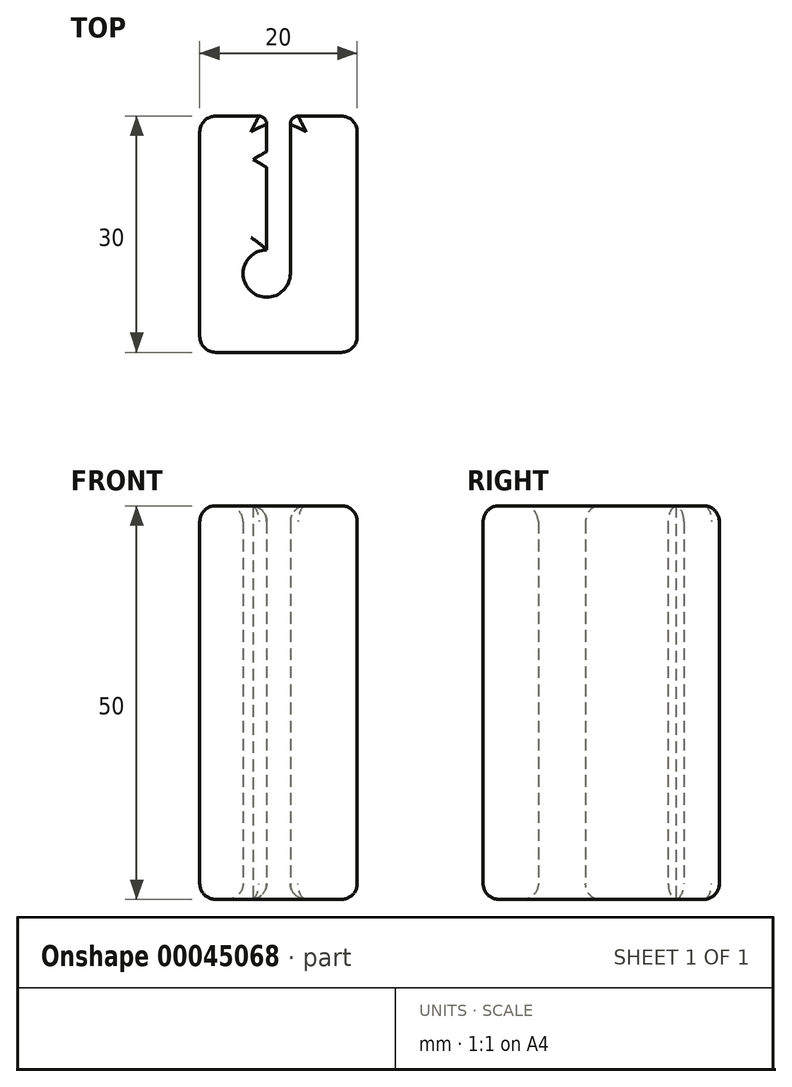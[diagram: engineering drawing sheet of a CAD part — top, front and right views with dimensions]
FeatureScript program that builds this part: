
annotation { "Feature Type Name" : "Feature", "Feature Type Description" : "" }
export const myFeature = defineFeature(function(context is Context, id is Id, definition is map)
    precondition{}
    {
        {
            var Q0;
            Q0=qCreatedBy(makeId("Top.planeOp"),FACE);
            var sketch = newSketch(context, id + "F0", { "sketchPlane" : qUnion([Q0])});
            skLineSegment(sketch, "E0.rect.bottom", {"start": v(8, -15) * mm, "end": v(-8, -15) * mm});
            skLineSegment(sketch, "E0.rect.left", {"start": v(10, -13) * mm, "end": v(10, 13) * mm});
            skLineSegment(sketch, "E0.rect.right", {"start": v(-10, -13) * mm, "end": v(-10, 13) * mm});
            skPoint(sketch, "E0.rect.middle", {"position": v(0, 0) * mm});
            skLineSegment(sketch, "E1.left", {"start": v(-1.5, 14) * mm, "end": v(-1.5, 10.5) * mm});
            skLineSegment(sketch, "E1.right", {"start": v(1.5, 14) * mm, "end": v(1.5, -5) * mm});
            skArc(sketch, "E2", {"start": v(-1.5, -2) * mm, "mid": v(-3.62, -7.12) * mm, "end": v(1.5, -5) * mm});
            skLineSegment(sketch, "E3", {"start": v(2.5, 15) * mm, "end": v(8, 15) * mm});
            skLineSegment(sketch, "E4", {"start": v(-2.5, 15) * mm, "end": v(-8, 15) * mm});
            skPoint(sketch, "E5.visualSharp", {"position": v(-10, 15) * mm});
            skArc(sketch, "E5.filletArc", {"start": v(-8, 15) * mm, "mid": v(-9.41, 14.41) * mm, "end": v(-10, 13) * mm});
            skPoint(sketch, "E6.visualSharp", {"position": v(-10, -15) * mm});
            skArc(sketch, "E6.filletArc", {"start": v(-10, -13) * mm, "mid": v(-9.41, -14.41) * mm, "end": v(-8, -15) * mm});
            skPoint(sketch, "E7.visualSharp", {"position": v(10, -15) * mm});
            skArc(sketch, "E7.filletArc", {"start": v(8, -15) * mm, "mid": v(9.41, -14.41) * mm, "end": v(10, -13) * mm});
            skPoint(sketch, "E8.visualSharp", {"position": v(10, 15) * mm});
            skArc(sketch, "E8.filletArc", {"start": v(10, 13) * mm, "mid": v(9.41, 14.41) * mm, "end": v(8, 15) * mm});
            skPoint(sketch, "E9.visualSharp", {"position": v(1.5, 15) * mm});
            skArc(sketch, "E9.filletArc", {"start": v(2.5, 15) * mm, "mid": v(1.8, 14.7) * mm, "end": v(1.5, 14) * mm});
            skPoint(sketch, "E10.visualSharp", {"position": v(-1.5, 15) * mm});
            skArc(sketch, "E10.filletArc", {"start": v(-1.5, 14) * mm, "mid": v(-1.8, 14.7) * mm, "end": v(-2.5, 15) * mm});
            skPoint(sketch, "E11", {"position": v(-1.5, 10.5) * mm});
            skLineSegment(sketch, "E12", {"start": v(-1.5, 10.5) * mm, "end": v(-3.23, 9.5) * mm});
            skLineSegment(sketch, "E13", {"start": v(-3.23, 9.5) * mm, "end": v(-1.5, 8.5) * mm});
            skLineSegment(sketch, "E14.trimOffspring", {"start": v(-1.5, 8.5) * mm, "end": v(-1.5, -2) * mm});
            skSolve(sketch);
        }
        {
            var Q0;
            Q0=makeQuery(id+"F0.imprint","IMPRINT",FACE,{"disambiguationData":[TD([[makeQuery(id+"F0.imprint","IMPRINT",EDGE,{"derivedFrom":sQuery(id+"F0.wireOp",EDGE,"E0.rect.bottom")}),-1.0]])]});
            extrude(context, id + "F1", {"entities" : qUnion([Q0]), "depth" : 50 * mm});
        }
        {
            var Q0;
            Q0=makeQuery(id+"F1.opExtrude","CAP_EDGE",EDGE,{"disambiguationData":[OSD([sQuery(id+"F0.wireOp",EDGE,"E0.rect.left")])],"isStart":false});
            var Q1;
            Q1=makeQuery(id+"F1.opExtrude","CAP_EDGE",EDGE,{"disambiguationData":[OSD([sQuery(id+"F0.wireOp",EDGE,"E0.rect.right")])],"isStart":true});
            fillet(context, id + "F2", {"entities" : qUnion([Q0, Q1]), "radius" : 2 * mm, "tangentPropagation" : true, "allowEdgeOverflow" : false});
        }
    });
